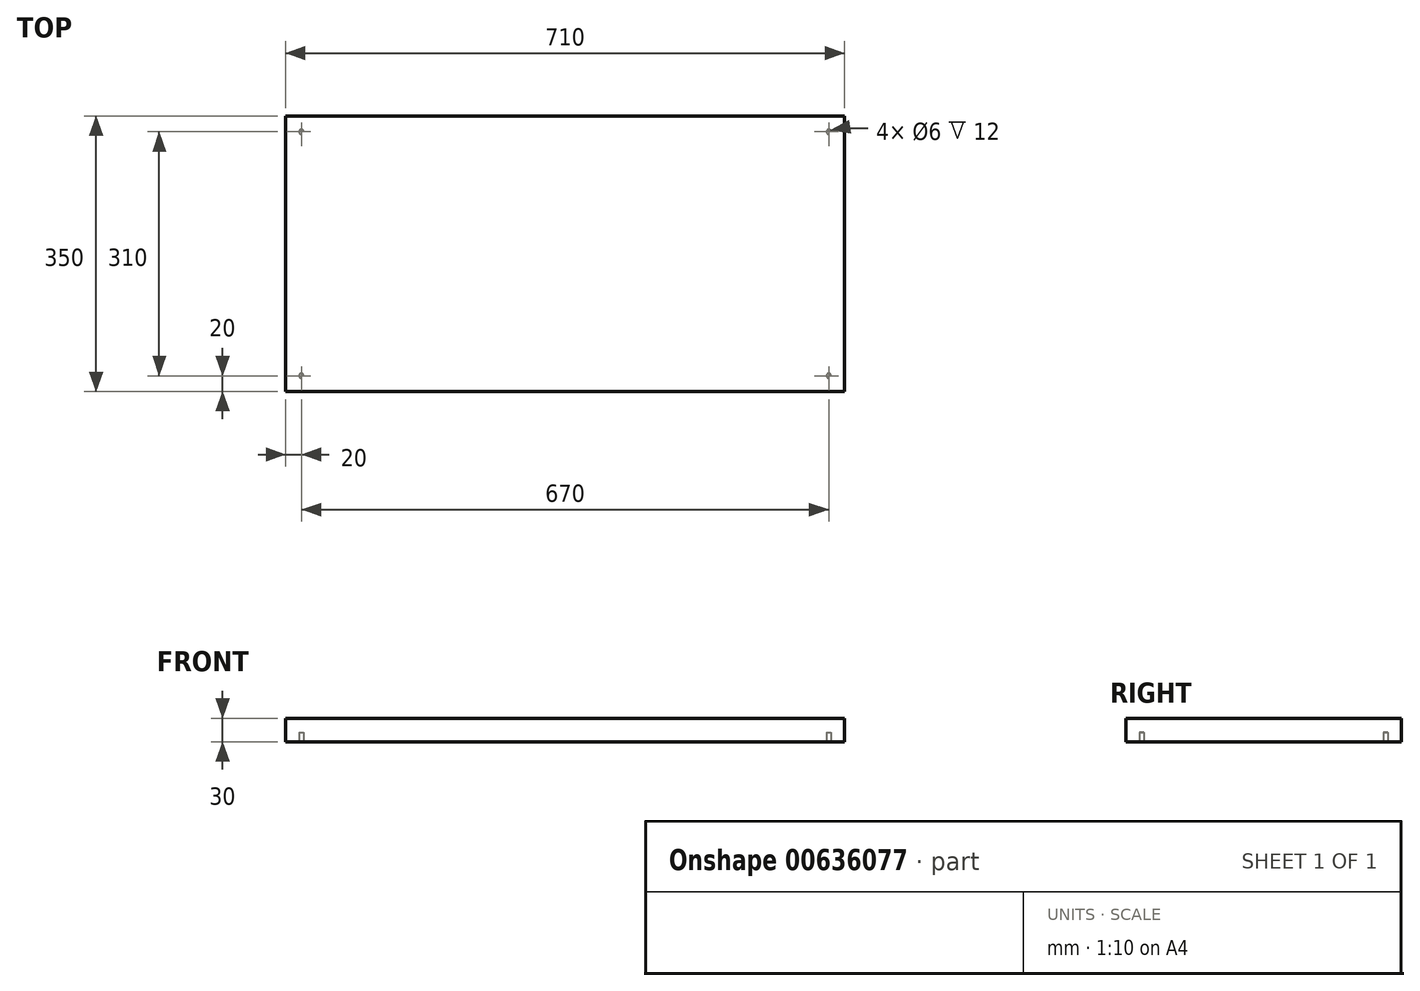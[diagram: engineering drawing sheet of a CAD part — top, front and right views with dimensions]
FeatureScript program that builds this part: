
annotation { "Feature Type Name" : "Feature", "Feature Type Description" : "" }
export const myFeature = defineFeature(function(context is Context, id is Id, definition is map)
    precondition{}
    {
        {
            var Q0;
            Q0=qCreatedBy(makeId("Top.planeOp"),FACE);
            var sketch = newSketch(context, id + "F0", { "sketchPlane" : qUnion([Q0])});
            skLineSegment(sketch, "E0.bottom", {"start": v(0, 0) * mm, "end": v(710, 0) * mm});
            skLineSegment(sketch, "E0.top", {"start": v(0, 350) * mm, "end": v(710, 350) * mm});
            skLineSegment(sketch, "E0.left", {"start": v(0, 0) * mm, "end": v(0, 350) * mm});
            skLineSegment(sketch, "E0.right", {"start": v(710, 0) * mm, "end": v(710, 350) * mm});
            skSolve(sketch);
        }
        {
            var Q0;
            Q0 = qSketchRegion(id + "F0", true);
            extrude(context, id + "F1", {"entities" : qUnion([Q0]), "depth" : 30 * mm, "offsetDistance" : 25.4 * mm});
        }
        {
            var Q0;
            Q0=makeQuery(id+"F1.opExtrude","CAP_FACE",FACE,{"disambiguationData":[OSD([sQuery(id+"F0.wireOp",EDGE,"E0.bottom"),sQuery(id+"F0.wireOp",EDGE,"E0.top"),sQuery(id+"F0.wireOp",EDGE,"E0.left"),sQuery(id+"F0.wireOp",EDGE,"E0.right")])],"isStart":true});
            var sketch = newSketch(context, id + "F2", { "sketchPlane" : qUnion([Q0])});
            skCircle(sketch, "E1", {"center": v(20, -20) * mm, "radius": 3 * mm});
            skLineSegment(sketch, "E2", {"start": v(355, 0) * mm, "end": v(355, -350) * mm, "construction": true});
            skLineSegment(sketch, "E3", {"start": v(0, -175) * mm, "end": v(710, -175) * mm, "construction": true});
            skCircle(sketch, "E4.MirrorC", {"center": v(690, -20) * mm, "radius": 3 * mm});
            skCircle(sketch, "E5.MirrorC", {"center": v(690, -330) * mm, "radius": 3 * mm});
            skCircle(sketch, "E6.MirrorC", {"center": v(20, -330) * mm, "radius": 3 * mm});
            skSolve(sketch);
        }
        {
            var Q0;
            Q0 = qSketchRegion(id + "F2", true);
            extrude(context, id + "F3", {"entities" : qUnion([Q0]), "operationType" : NewBodyOperationType.REMOVE, "oppositeDirection" : true, "depth" : 12 * mm, "offsetDistance" : 25 * mm});
        }
        {
            var Q0;
            Q0=makeQuery(id+"F1.opExtrude","CAP_FACE",FACE,{"disambiguationData":[OSD([sQuery(id+"F0.wireOp",EDGE,"E0.bottom"),sQuery(id+"F0.wireOp",EDGE,"E0.top"),sQuery(id+"F0.wireOp",EDGE,"E0.left"),sQuery(id+"F0.wireOp",EDGE,"E0.right")])],"isStart":true});
            var sketch = newSketch(context, id + "F4", { "sketchPlane" : qUnion([Q0])});
            skCircle(sketch, "E7", {"center": v(20, -330) * mm, "radius": 3 * mm});
            skSolve(sketch);
        }
        {
            var Q0;
            Q0 = qSketchRegion(id + "F4", true);
            extrude(context, id + "F5", {"entities" : qUnion([Q0]), "operationType" : NewBodyOperationType.REMOVE, "oppositeDirection" : true, "depth" : 12 * mm, "offsetDistance" : 25 * mm});
        }
    });
